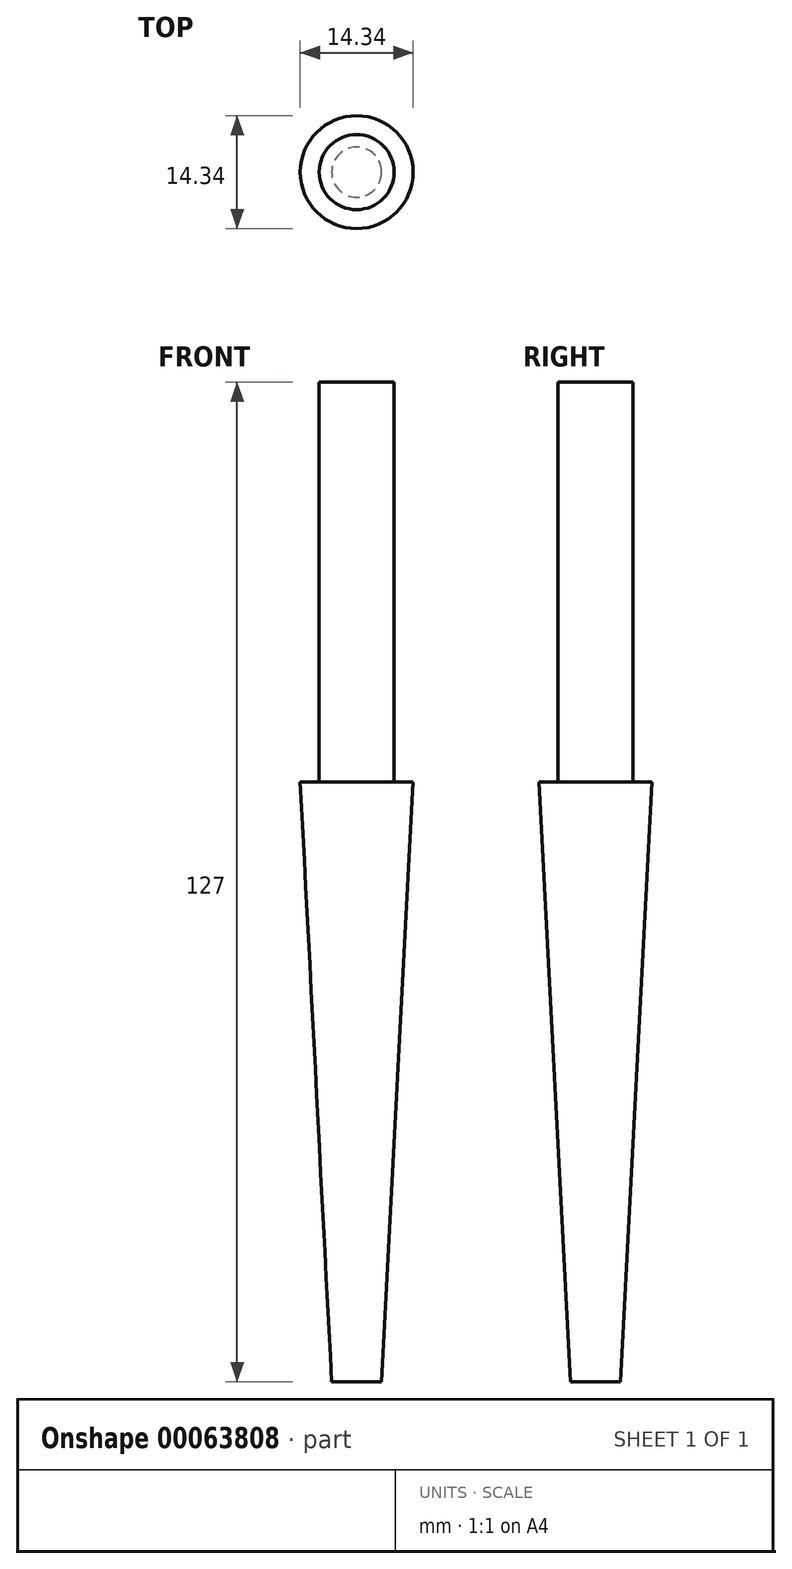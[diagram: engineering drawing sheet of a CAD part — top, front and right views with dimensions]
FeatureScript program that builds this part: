
annotation { "Feature Type Name" : "Feature", "Feature Type Description" : "" }
export const myFeature = defineFeature(function(context is Context, id is Id, definition is map)
    precondition{}
    {
        {
            var Q0;
            Q0=qCreatedBy(makeId("Front.planeOp"),FACE);
            var sketch = newSketch(context, id + "F0", { "sketchPlane" : qUnion([Q0])});
            skLineSegment(sketch, "E0", {"start": v(-3.17, 0) * mm, "end": v(3.17, 0) * mm});
            skLineSegment(sketch, "E1", {"start": v(3.17, 0) * mm, "end": v(7.17, 76.2) * mm});
            skLineSegment(sketch, "E2", {"start": v(-3.18, 0) * mm, "end": v(-7.17, 76.2) * mm});
            skLineSegment(sketch, "E3", {"start": v(0, 0) * mm, "end": v(0, 76.2) * mm, "construction": true});
            skLineSegment(sketch, "E4", {"start": v(-7.17, 76.2) * mm, "end": v(-4.76, 76.2) * mm});
            skLineSegment(sketch, "E5", {"start": v(-4.76, 76.2) * mm, "end": v(-4.76, 127) * mm});
            skLineSegment(sketch, "E6", {"start": v(-4.76, 127) * mm, "end": v(4.76, 127) * mm});
            skLineSegment(sketch, "E7", {"start": v(4.76, 127) * mm, "end": v(4.76, 76.2) * mm});
            skLineSegment(sketch, "E8", {"start": v(4.76, 76.2) * mm, "end": v(7.17, 76.2) * mm});
            skSolve(sketch);
        }
        {
            var Q0;
            Q0=qCreatedBy(makeId("Front.planeOp"),FACE);
            var sketch = newSketch(context, id + "F1", { "sketchPlane" : qUnion([Q0])});
            skLineSegment(sketch, "E9", {"start": v(-3.18, 0) * mm, "end": v(-7.17, 76.2) * mm});
            skLineSegment(sketch, "E10", {"start": v(-7.17, 76.2) * mm, "end": v(-4.76, 76.2) * mm});
            skLineSegment(sketch, "E11", {"start": v(-4.76, 76.2) * mm, "end": v(-4.76, 127) * mm});
            skLineSegment(sketch, "E12", {"start": v(-4.76, 127) * mm, "end": v(0, 127) * mm});
            skLineSegment(sketch, "E13", {"start": v(-3.18, 0) * mm, "end": v(0, 0) * mm});
            skLineSegment(sketch, "E14", {"start": v(0, 127) * mm, "end": v(0, 0) * mm});
            skSolve(sketch);
        }
        {
            var Q0;
            Q0 = qSketchRegion(id + "F1", true);
            var Q1;
            Q1=sQuery(id+"F0.wireOp",EDGE,"E3");
            revolve(context, id + "F2", {"entities" : qUnion([Q0]), "axis" : qUnion([Q1]), "revolveType" : RevolveType.FULL});
        }
    });
